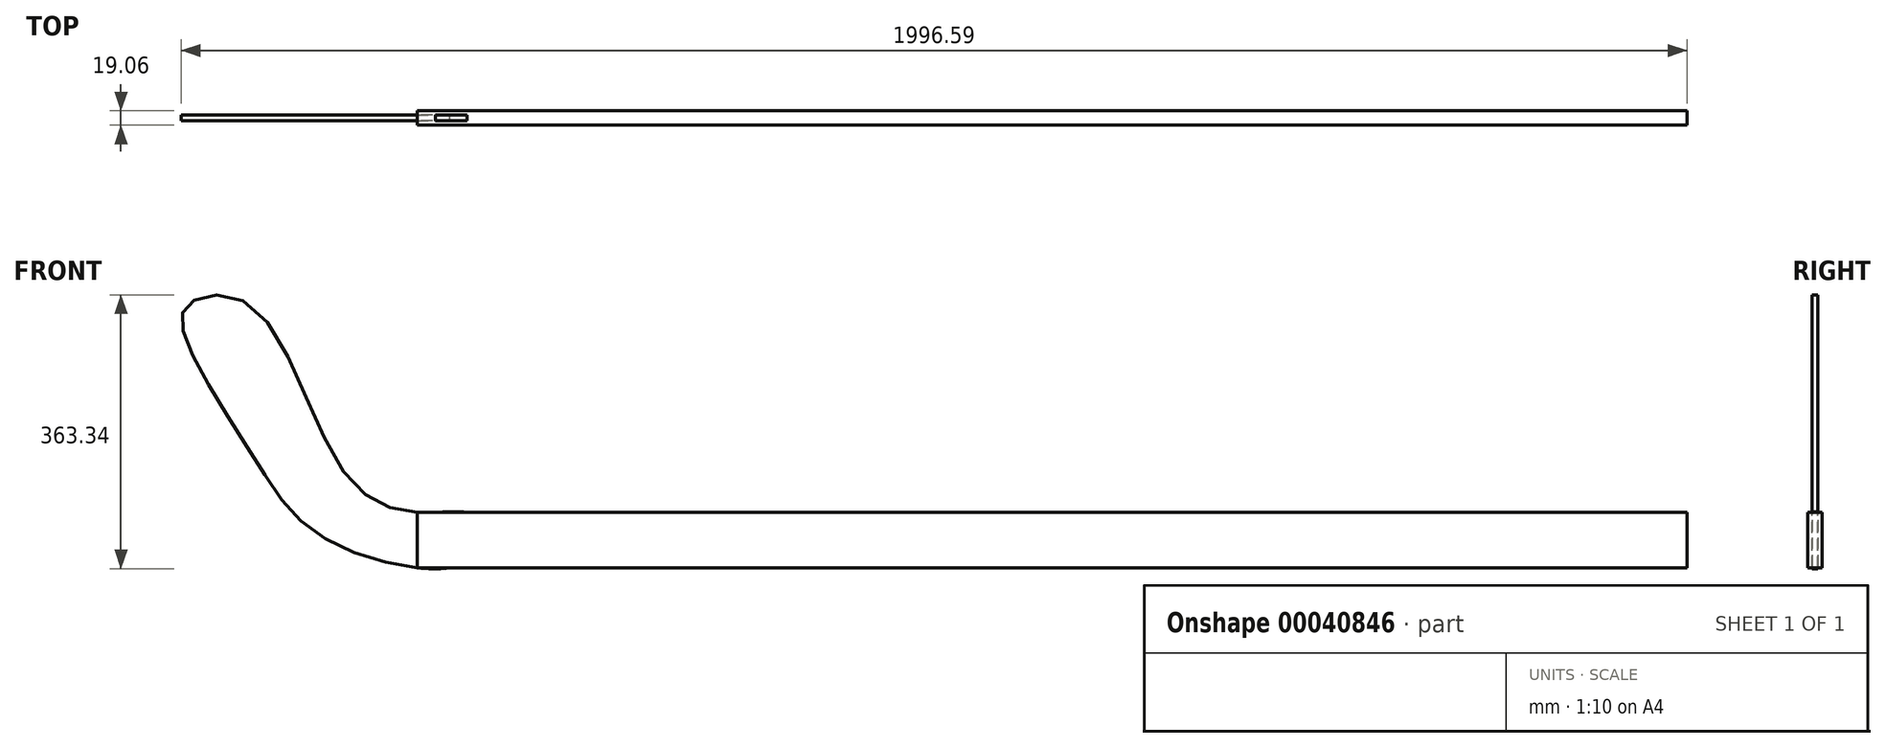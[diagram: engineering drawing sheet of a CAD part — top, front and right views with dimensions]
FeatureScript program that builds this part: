
annotation { "Feature Type Name" : "Feature", "Feature Type Description" : "" }
export const myFeature = defineFeature(function(context is Context, id is Id, definition is map)
    precondition{}
    {
        {
            var Q0;
            Q0=qCreatedBy(makeId("Front.planeOp"),FACE);
            var sketch = newSketch(context, id + "F0", { "sketchPlane" : qUnion([Q0])});
            skLineSegment(sketch, "E0.left", {"start": v(-298.88, -96.7) * mm, "end": v(-298.88, -23.17) * mm});
            skLineSegment(sketch, "E0.right", {"start": v(1584.08, -69.68) * mm, "end": v(1584.08, -23.17) * mm});
            skFitSpline(sketch, "E1", {"points": [v(-298.88, -23.17) * mm, v(-400.72, 37.02) * mm, v(-519.3, 251) * mm, v(-601.8, 253.58) * mm, v(-606.96, 209.75) * mm, v(-521.89, 60.23) * mm, v(-439.39, -45.47) * mm, v(-298.88, -96.7) * mm, v(-214.74, -77.25) * mm, v(-213.13, -30.74) * mm, v(-298.88, -23.17) * mm]});
            skSolve(sketch);
        }
        {
            var Q0;
            {var subQ1=sQuery(id+"F0.wireOp",EDGE,"E0.left");Q0=makeQuery(id+"F0.imprint","IMPRINT",FACE,{"disambiguationData":[TD([[makeQuery(id+"F0.imprint","IMPRINT",EDGE,{"derivedFrom":subQ1}),1.0]])]});}
            var Q1;
            {var subQ5=sQuery(id+"F0.wireOp",EDGE,"E0.left");Q1=makeQuery(id+"F0.imprint","IMPRINT",FACE,{"disambiguationData":[TD([[makeQuery(id+"F0.imprint","IMPRINT",EDGE,{"derivedFrom":subQ5}),-1.0]])]});}
            extrude(context, id + "F1", {"entities" : qUnion([Q0, Q1]), "depth" : 3.8 * mm, "hasSecondDirection" : true, "secondDirectionOppositeDirection" : true, "secondDirectionDepth" : 3.8 * mm});
        }
        {
            var Q0;
            Q0=qCreatedBy(makeId("Front.planeOp"),FACE);
            var sketch = newSketch(context, id + "F2", { "sketchPlane" : qUnion([Q0])});
            skLineSegment(sketch, "E2.bottom", {"start": v(-298.88, -23.17) * mm, "end": v(1385.15, -23.17) * mm});
            skLineSegment(sketch, "E2.top", {"start": v(-298.88, -96.7) * mm, "end": v(1385.15, -96.7) * mm});
            skLineSegment(sketch, "E2.left", {"start": v(-298.88, -23.17) * mm, "end": v(-298.88, -96.7) * mm});
            skLineSegment(sketch, "E2.right", {"start": v(1385.15, -23.17) * mm, "end": v(1385.15, -96.7) * mm});
            skSolve(sketch);
        }
        {
            var Q0;
            Q0 = qSketchRegion(id + "F2", true);
            extrude(context, id + "F3", {"entities" : qUnion([Q0]), "operationType" : NewBodyOperationType.ADD, "depth" : 9.52 * mm, "hasSecondDirection" : true, "secondDirectionOppositeDirection" : true, "secondDirectionDepth" : 9.52 * mm});
        }
    });
